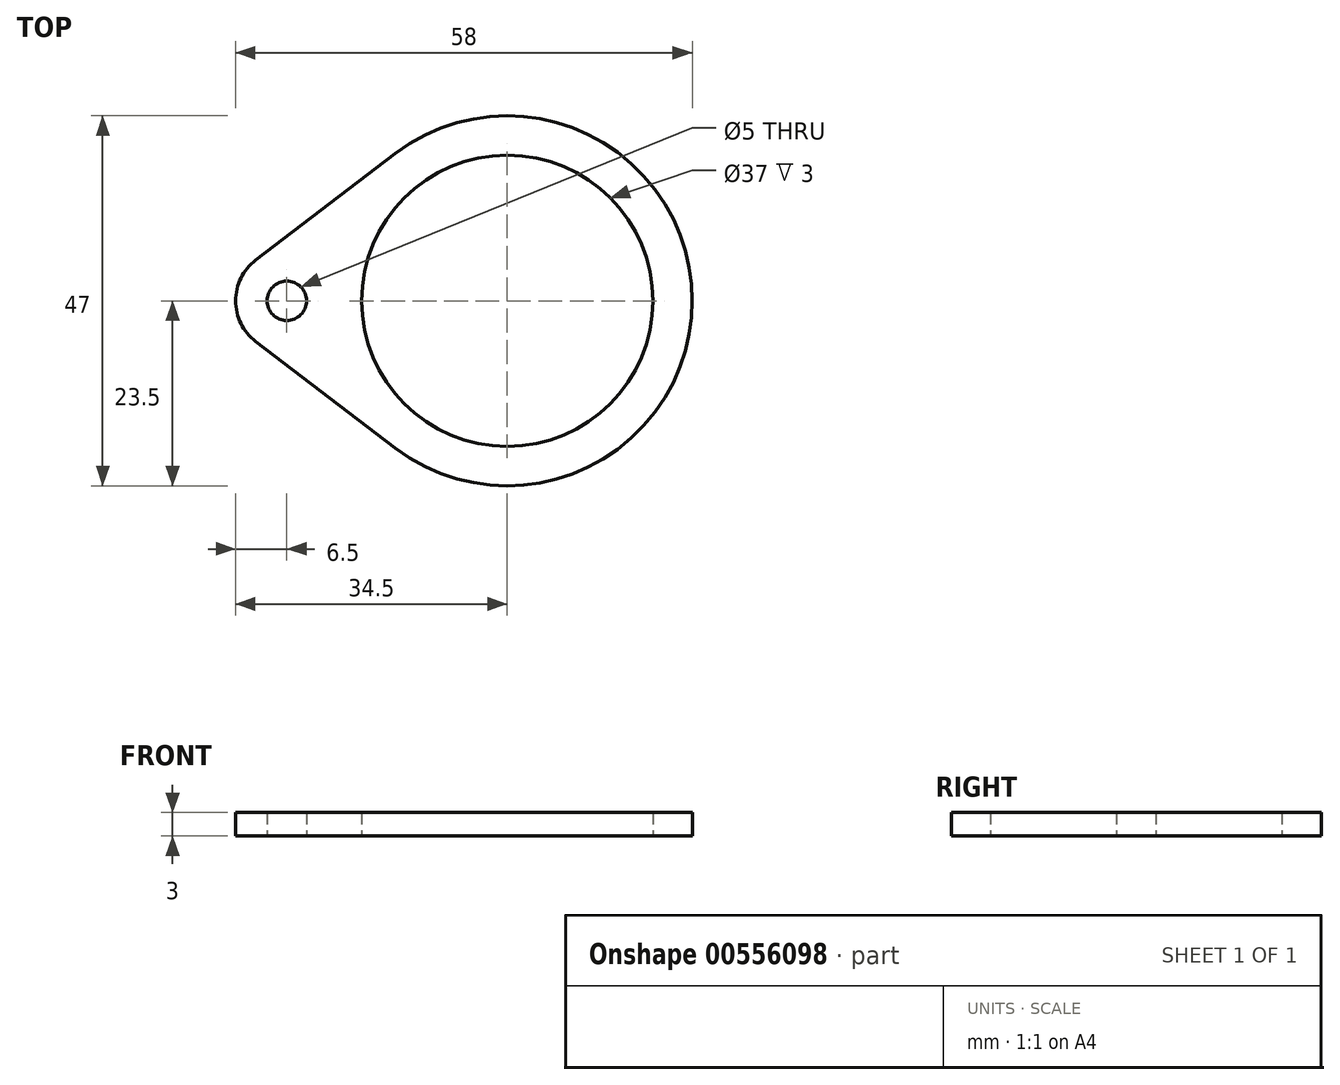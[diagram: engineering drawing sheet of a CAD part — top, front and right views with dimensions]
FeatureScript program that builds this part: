
annotation { "Feature Type Name" : "Feature", "Feature Type Description" : "" }
export const myFeature = defineFeature(function(context is Context, id is Id, definition is map)
    precondition{}
    {
        {
            var Q0;
            Q0=qCreatedBy(makeId("Top.planeOp"),FACE);
            var sketch = newSketch(context, id + "F0", { "sketchPlane" : qUnion([Q0])});
            skCircle(sketch, "E0", {"center": v(0, 0) * mm, "radius": 23.5 * mm});
            skCircle(sketch, "E1", {"center": v(0, 0) * mm, "radius": 18.5 * mm});
            skCircle(sketch, "E2", {"center": v(-28, 0) * mm, "radius": 2.5 * mm});
            skCircle(sketch, "E3", {"center": v(-28, 0) * mm, "radius": 6.5 * mm});
            skLineSegment(sketch, "E4", {"start": v(-28, 0) * mm, "end": v(0, 0) * mm});
            skLineSegment(sketch, "E5", {"start": v(-31.95, 5.16) * mm, "end": v(-14.27, 18.67) * mm});
            skLineSegment(sketch, "E6", {"start": v(-31.95, -5.16) * mm, "end": v(-14.27, -18.67) * mm});
            skSolve(sketch);
        }
        {
            var Q0;
            Q0=makeQuery(id+"F0.imprint","IMPRINT",FACE,{"disambiguationData":[TD([[makeQuery(id+"F0.imprint","IMPRINT",EDGE,{"derivedFrom":sQuery(id+"F0.wireOp",EDGE,"E2")}),-1.0]])]});
            var Q1;
            {var subQ0=sQuery(id+"F0.wireOp",EDGE,"E5");Q1=makeQuery(id+"F0.imprint","IMPRINT",FACE,{"disambiguationData":[TD([[makeQuery(id+"F0.imprint","IMPRINT",EDGE,{"derivedFrom":subQ0}),-1.0]])]});}
            var Q2;
            {var subQ0=sQuery(id+"F0.wireOp",EDGE,"E6");Q2=makeQuery(id+"F0.imprint","IMPRINT",FACE,{"disambiguationData":[TD([[makeQuery(id+"F0.imprint","IMPRINT",EDGE,{"derivedFrom":subQ0}),1.0]])]});}
            var Q3;
            {var subQ0=sQuery(id+"F0.wireOp",EDGE,"E4");var subQ1=sQuery(id+"F0.wireOp",EDGE,"E0");var subQ2=makeQuery(id+"F0.imprint","INTERSECT",VERTEX,{"derivedFrom":[subQ1,subQ0]});Q3=makeQuery(id+"F0.imprint","IMPRINT",FACE,{"disambiguationData":[TD([[makeQuery(id+"F0.imprint","IMPRINT",EDGE,{"disambiguationData":[TD([[subQ2,-1.0]])],"derivedFrom":subQ1}),1.0]])]});}
            var Q4;
            {var subQ0=sQuery(id+"F0.wireOp",EDGE,"E4");var subQ1=sQuery(id+"F0.wireOp",EDGE,"E0");var subQ2=makeQuery(id+"F0.imprint","INTERSECT",VERTEX,{"derivedFrom":[subQ1,subQ0]});Q4=makeQuery(id+"F0.imprint","IMPRINT",FACE,{"disambiguationData":[TD([[makeQuery(id+"F0.imprint","IMPRINT",EDGE,{"disambiguationData":[TD([[subQ2,1.0]])],"derivedFrom":subQ1}),1.0]])]});}
            var Q5;
            Q5=makeQuery(id+"F0.imprint","IMPRINT",FACE,{"disambiguationData":[TD([[makeQuery(id+"F0.imprint","IMPRINT",EDGE,{"derivedFrom":sQuery(id+"F0.wireOp",EDGE,"E1")}),-1.0]])]});
            extrude(context, id + "F1", {"entities" : qUnion([Q0, Q1, Q2, Q3, Q4, Q5]), "depth" : 3 * mm, "offsetDistance" : 25.4 * mm});
        }
    });
